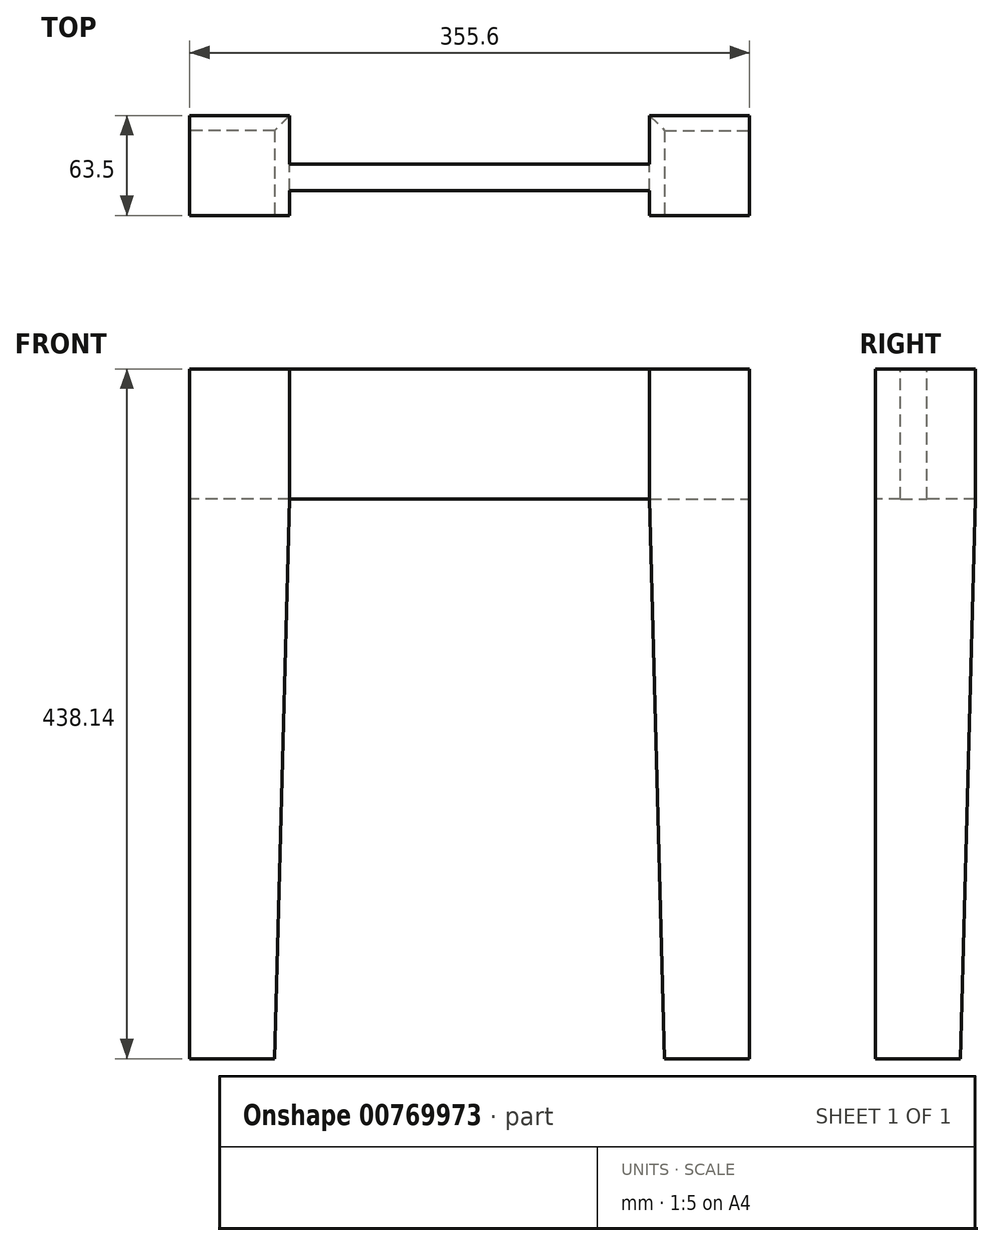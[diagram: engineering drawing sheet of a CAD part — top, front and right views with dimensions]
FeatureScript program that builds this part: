
annotation { "Feature Type Name" : "Feature", "Feature Type Description" : "" }
export const myFeature = defineFeature(function(context is Context, id is Id, definition is map)
    precondition{}
    {
        {
            var Q0;
            Q0=qCreatedBy(makeId("Front.planeOp"),FACE);
            var sketch = newSketch(context, id + "F0", { "sketchPlane" : qUnion([Q0])});
            skLineSegment(sketch, "E0.bottom", {"start": v(31.75, -219.08) * mm, "end": v(-31.75, -219.08) * mm});
            skLineSegment(sketch, "E0.top", {"start": v(31.75, 219.08) * mm, "end": v(-31.75, 219.08) * mm});
            skLineSegment(sketch, "E0.left", {"start": v(31.75, -219.08) * mm, "end": v(31.75, 219.08) * mm});
            skLineSegment(sketch, "E0.right", {"start": v(-31.75, -219.08) * mm, "end": v(-31.75, 219.08) * mm});
            skPoint(sketch, "E0.middle", {"position": v(0, 0) * mm});
            skLineSegment(sketch, "E1", {"start": v(31.75, 219.08) * mm, "end": v(31.75, 136.53) * mm});
            skLineSegment(sketch, "E2", {"start": v(-31.75, -219.08) * mm, "end": v(22.23, -219.08) * mm});
            skLineSegment(sketch, "E3", {"start": v(22.23, -219.08) * mm, "end": v(31.75, 136.53) * mm});
            skSolve(sketch);
        }
        {
            var Q0;
            {var subQ1=sQuery(id+"F0.wireOp",EDGE,"E0.top");Q0=makeQuery(id+"F0.imprint","IMPRINT",FACE,{"disambiguationData":[TD([[makeQuery(id+"F0.imprint","IMPRINT",EDGE,{"derivedFrom":subQ1}),1.0]])]});}
            extrude(context, id + "F1", {"entities" : qUnion([Q0]), "depth" : 63.5 * mm, "offsetDistance" : 25.4 * mm});
        }
        {
            var Q0;
            Q0=makeQuery(id+"F1.opExtrude","SWEPT_FACE",FACE,{"disambiguationData":[OSD([sQuery(id+"F0.wireOp",EDGE,"E0.right")])]});
            var sketch = newSketch(context, id + "F2", { "sketchPlane" : qUnion([Q0])});
            skLineSegment(sketch, "E4", {"start": v(0, 219.08) * mm, "end": v(0, 136.53) * mm});
            skLineSegment(sketch, "E5", {"start": v(63.5, -219.08) * mm, "end": v(9.52, -219.08) * mm});
            skLineSegment(sketch, "E6", {"start": v(0, 136.53) * mm, "end": v(9.52, -219.08) * mm});
            skSolve(sketch);
        }
        {
            var Q0;
            {var subQ0=sQuery(id+"F2.wireOp",EDGE,"E6");Q0=makeQuery(id+"F2.imprint","IMPRINT",FACE,{"disambiguationData":[TD([[makeQuery(id+"F2.imprint","IMPRINT",EDGE,{"derivedFrom":subQ0}),-1.0]])]});}
            extrude(context, id + "F3", {"entities" : qUnion([Q0]), "operationType" : NewBodyOperationType.REMOVE, "oppositeDirection" : true, "depth" : 63.5 * mm, "offsetDistance" : 25.4 * mm});
        }
        {
            var Q0;
            Q0=makeQuery(id+"F1.opExtrude","SWEPT_FACE",FACE,{"disambiguationData":[OSD([sQuery(id+"F0.wireOp",EDGE,"E0.top")])]});
            var sketch = newSketch(context, id + "F4", { "sketchPlane" : qUnion([Q0])});
            skLineSegment(sketch, "E7", {"start": v(31.75, -63.5) * mm, "end": v(31.75, -47.62) * mm});
            skLineSegment(sketch, "E8.bottom", {"start": v(31.75, -47.62) * mm, "end": v(260.35, -47.62) * mm});
            skLineSegment(sketch, "E8.top", {"start": v(31.75, -30.93) * mm, "end": v(260.35, -30.93) * mm});
            skLineSegment(sketch, "E8.left", {"start": v(31.75, -47.62) * mm, "end": v(31.75, -30.93) * mm});
            skLineSegment(sketch, "E8.right", {"start": v(260.35, -47.62) * mm, "end": v(260.35, -30.93) * mm});
            skSolve(sketch);
        }
        {
            var Q0;
            Q0=makeQuery(id+"F1.opExtrude","SWEPT_BODY",BODY,{"disambiguationData":[OSD([sQuery(id+"F0.wireOp",EDGE,"E0.bottom"),sQuery(id+"F0.wireOp",EDGE,"E0.top"),sQuery(id+"F0.wireOp",EDGE,"E0.left"),sQuery(id+"F0.wireOp",EDGE,"E0.right"),sQuery(id+"F0.wireOp",EDGE,"E3")])]});
            var Q1;
            Q1=qCreatedBy(makeId("Right.planeOp"),FACE);
            mirror(context, id + "F5", {"operationType" : NewBodyOperationType.ADD, "entities" : qUnion([Q0]), "mirrorPlane" : qUnion([Q1])});
        }
        {
            var Q0;
            Q0=makeQuery(id+"F4.imprint","IMPRINT",FACE,{"disambiguationData":[TD([[makeQuery(id+"F4.imprint","IMPRINT",EDGE,{"derivedFrom":sQuery(id+"F4.wireOp",EDGE,"E8.bottom")}),1.0]])]});
            extrude(context, id + "F6", {"entities" : qUnion([Q0]), "operationType" : NewBodyOperationType.ADD, "depth" : -82.55 * mm, "offsetDistance" : 25.4 * mm});
        }
        {
            var Q0;
            Q0=makeQuery(id+"F6.opExtrude","CAP_EDGE",EDGE,{"disambiguationData":[OSD([sQuery(id+"F4.wireOp",EDGE,"E8.bottom")])],"isStart":true});
            cPoint(context, id + "F7", {"entities" : qUnion([Q0]), "parameter" : 0.5});
        }
        {
            var Q0;
            Q0=makeQuery(id+"F6.opExtrude","CAP_EDGE",EDGE,{"disambiguationData":[OSD([sQuery(id+"F4.wireOp",EDGE,"E8.top")])],"isStart":true});
            cPoint(context, id + "F8", {"entities" : qUnion([Q0]), "parameter" : 0.5});
        }
        {
            var Q0;
            Q0=makeQuery(id+"F6.opExtrude","CAP_EDGE",EDGE,{"disambiguationData":[OSD([sQuery(id+"F4.wireOp",EDGE,"E8.bottom")])],"isStart":false});
            cPoint(context, id + "F9", {"entities" : qUnion([Q0]), "parameter" : 0.5});
        }
        {
            var Q0;
            Q0 = qCreatedBy(id + "F7" ,VERTEX);
            var Q1;
            Q1 = qCreatedBy(id + "F8" ,VERTEX);
            var Q2;
            Q2 = qCreatedBy(id + "F9" ,VERTEX);
            cPlane(context, id + "F10", {"entities" : qUnion([Q0, Q1, Q2]), "cplaneType" : CPlaneType.THREE_POINT, "offset" : 25.4 * mm, "width" : 152.4 * mm, "height" : 152.4 * mm});
        }
        {
            var Q0;
            {var subQ0=makeQuery(id+"F1.opExtrude","CAP_FACE",FACE,{"disambiguationData":[OSD([sQuery(id+"F0.wireOp",EDGE,"E0.bottom"),sQuery(id+"F0.wireOp",EDGE,"E0.top"),sQuery(id+"F0.wireOp",EDGE,"E0.left"),sQuery(id+"F0.wireOp",EDGE,"E0.right"),sQuery(id+"F0.wireOp",EDGE,"E3")])],"isStart":false});Q0=makeQuery(id+"F5.boolean.opBoolean","MERGE",FACE,{"derivedFrom":[subQ0,makeQuery(id+"F5.opPattern","COPY",FACE,{"derivedFrom":subQ0,"instanceName":"1"})]});}
            var sketch = newSketch(context, id + "F11", { "sketchPlane" : qUnion([Q0])});
            skLineSegment(sketch, "E9", {"start": v(31.75, 219.08) * mm, "end": v(31.75, 136.53) * mm});
            skLineSegment(sketch, "E10", {"start": v(-31.75, -219.08) * mm, "end": v(22.23, -219.08) * mm});
            skLineSegment(sketch, "E11", {"start": v(22.23, -219.08) * mm, "end": v(31.75, 136.53) * mm});
            skSolve(sketch);
        }
        {
            var Q0;
            {var subQ0=sQuery(id+"F11.wireOp",EDGE,"E11");Q0=makeQuery(id+"F11.imprint","IMPRINT",FACE,{"disambiguationData":[TD([[makeQuery(id+"F11.imprint","IMPRINT",EDGE,{"derivedFrom":subQ0}),-1.0]])]});}
            extrude(context, id + "F12", {"entities" : qUnion([Q0]), "operationType" : NewBodyOperationType.REMOVE, "oppositeDirection" : true, "depth" : 63.5 * mm, "offsetDistance" : 25.4 * mm});
        }
        {
            var Q0;
            Q0=makeQuery(id+"F1.opExtrude","SWEPT_BODY",BODY,{"disambiguationData":[OSD([sQuery(id+"F0.wireOp",EDGE,"E0.bottom"),sQuery(id+"F0.wireOp",EDGE,"E0.top"),sQuery(id+"F0.wireOp",EDGE,"E0.left"),sQuery(id+"F0.wireOp",EDGE,"E0.right"),sQuery(id+"F0.wireOp",EDGE,"E3")])]});
            var Q1;
            Q1=qCreatedBy(id+"F10.planeOp",FACE);
            mirror(context, id + "F13", {"operationType" : NewBodyOperationType.ADD, "entities" : qUnion([Q0]), "mirrorPlane" : qUnion([Q1])});
        }
    });
